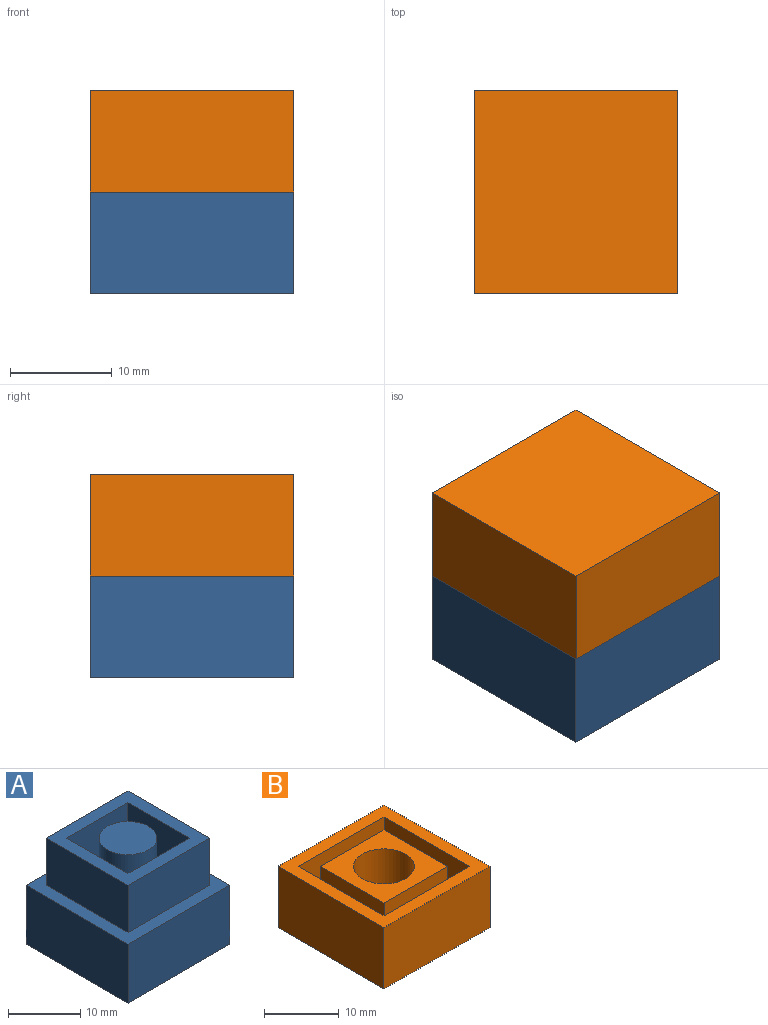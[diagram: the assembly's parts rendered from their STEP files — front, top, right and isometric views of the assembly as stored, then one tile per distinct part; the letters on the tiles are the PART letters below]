
ASSEMBLY  parts=2 mates=1
PART A: 18 faces, bbox 20x20x18 mm
  f0: plane 20x20mm, normal (0,0,1), area 144mm2, adj f1,f2,f3,f4,f6,f7,f8,f13
  f1: plane 20x10mm, normal (0,1,0), area 200mm2, adj f0,f2,f4,f5
  f2: plane 20x10mm, normal (-1,0,0), area 200mm2, adj f0,f1,f3,f5
  f3: plane 20x10mm, normal (0,-1,0), area 200mm2, adj f0,f2,f4,f5
  f4: plane 20x10mm, normal (1,0,0), area 200mm2, adj f0,f1,f3,f5
  f5: plane 20x20mm, normal (0,0,-1), area 400mm2, adj f1,f2,f3,f4
  f6: plane 16x8mm, normal (0,1,0), area 128mm2, adj f0,f7,f13,f14
  f7: plane 16x8mm, normal (-1,0,0), area 128mm2, adj f0,f6,f8,f14
  f8: plane 16x8mm, normal (0,-1,0), area 128mm2, adj f0,f7,f13,f14
  f9: plane 12x8mm, normal (1,0,0), area 96mm2, adj f10,f12,f14,f15
  f10: plane 12x8mm, normal (0,-1,0), area 96mm2, adj f9,f11,f14,f15
  f11: plane 12x8mm, normal (-1,0,0), area 96mm2, adj f10,f12,f14,f15
  f12: plane 12x8mm, normal (0,1,0), area 96mm2, adj f9,f11,f14,f15
  f13: plane 16x8mm, normal (1,0,0), area 128mm2, adj f0,f6,f8,f14
  f14: plane 16x16mm, normal (0,0,1), area 112mm2, adj f6,f7,f8,f9,f10,f11,f12,f13
  f15: plane 12x12mm, normal (0,0,1), area 93.7mm2, adj f9,f10,f11,f12,f16
  f16: cylinder r=4mm len=8mm, axis (0,0,-1), area 201.1mm2, adj f15,f17
  f17: plane 8x8mm, normal (0,0,1), area 50.3mm2, adj f16
PART B: 18 faces, bbox 20x20x10 mm
  f0: plane 20x20mm, normal (0,0,1), area 140.8mm2, adj f1,f2,f3,f4,f6,f7,f8,f13
  f1: plane 20x10mm, normal (0,1,0), area 200mm2, adj f0,f2,f4,f5
  f2: plane 20x10mm, normal (-1,0,0), area 200mm2, adj f0,f1,f3,f5
  f3: plane 20x10mm, normal (0,-1,0), area 200mm2, adj f0,f2,f4,f5
  f4: plane 20x10mm, normal (1,0,0), area 200mm2, adj f0,f1,f3,f5
  f5: plane 20x20mm, normal (0,0,-1), area 400mm2, adj f1,f2,f3,f4
  f6: plane 16.1x8.1mm, normal (0,-1,0), area 130.4mm2, adj f0,f7,f13,f14
  f7: plane 16.1x8.1mm, normal (1,0,0), area 130.4mm2, adj f0,f6,f8,f14
  f8: plane 16.1x8.1mm, normal (0,1,0), area 130.4mm2, adj f0,f7,f13,f14
  f9: plane 11.9x8.1mm, normal (-1,0,0), area 96.4mm2, adj f10,f12,f14,f15
  f10: plane 11.9x8.1mm, normal (0,1,0), area 96.4mm2, adj f9,f11,f14,f15
  f11: plane 11.9x8.1mm, normal (1,0,0), area 96.4mm2, adj f10,f12,f14,f15
  f12: plane 11.9x8.1mm, normal (0,-1,0), area 96.4mm2, adj f9,f11,f14,f15
  f13: plane 16.1x8.1mm, normal (-1,0,0), area 130.4mm2, adj f0,f6,f8,f14
  f14: plane 16.1x16.1mm, normal (0,0,1), area 117.6mm2, adj f6,f7,f8,f9,f10,f11,f12,f13
  f15: plane 11.9x11.9mm, normal (0,0,1), area 90.1mm2, adj f9,f10,f11,f12,f16
  f16: cylinder r=4.05mm len=8.1mm, axis (0,0,1), area 206.1mm2, adj f15,f17
  f17: plane 8.1x8.1mm, normal (0,0,1), area 51.5mm2, adj f16
PLACE A t=(21.5,13.16,-4)mm
PLACE B rot(axis=(1,0,0),180deg) t=(-5.97,-46.55,16)mm
MATE fastened B.f16 <-> A.f16  axis (0,0,-1) through (-36.2,-17.5,14.1)mm
